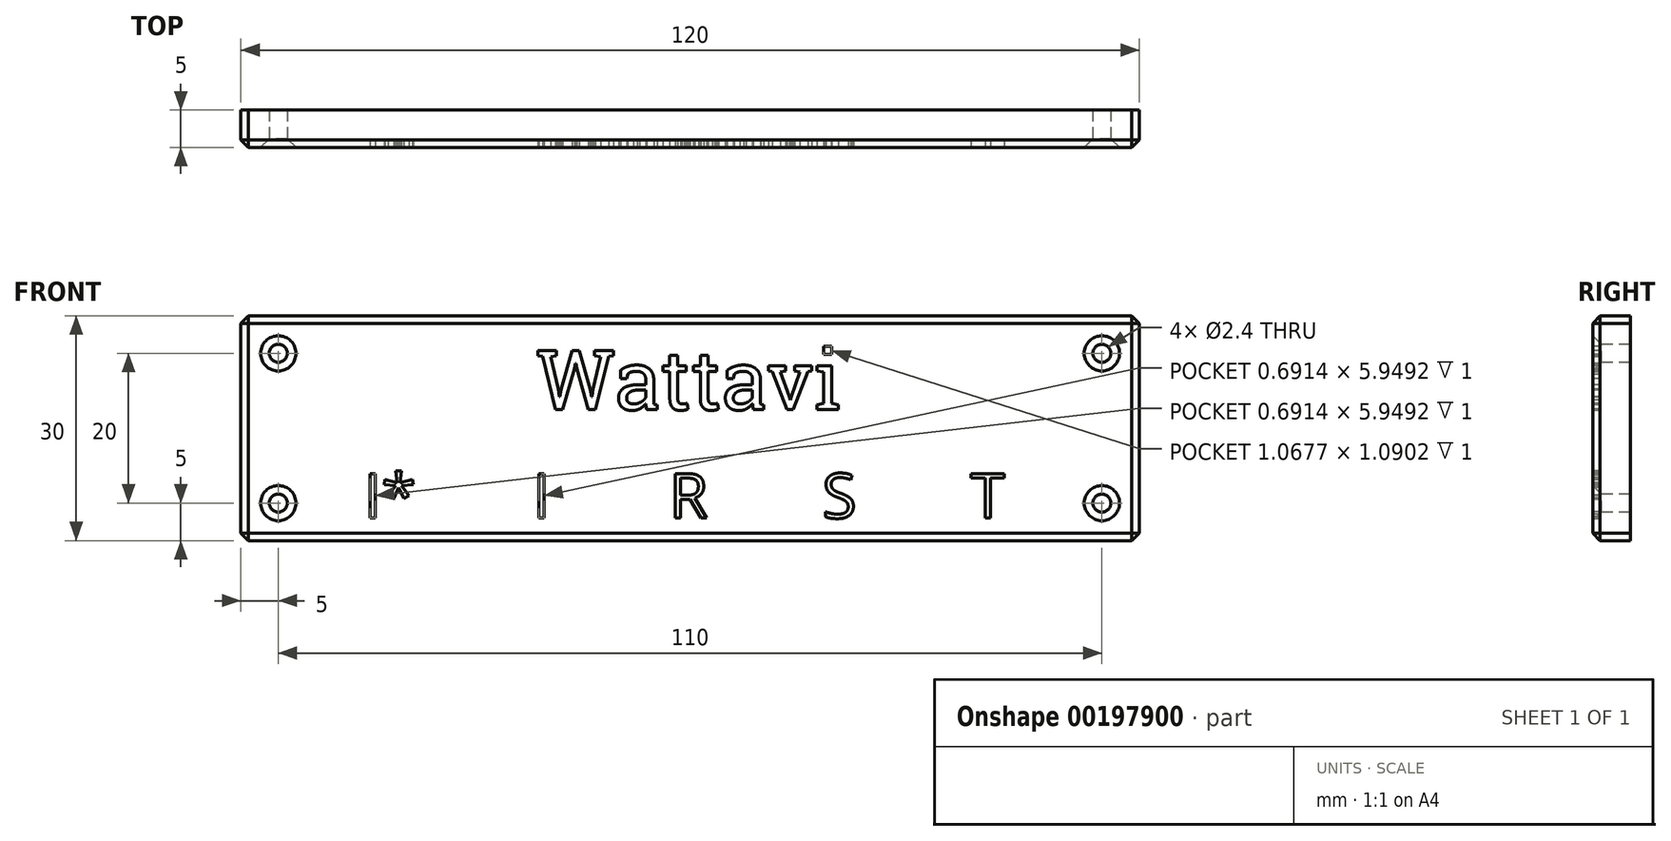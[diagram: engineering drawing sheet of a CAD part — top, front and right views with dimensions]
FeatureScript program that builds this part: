
annotation { "Feature Type Name" : "Feature", "Feature Type Description" : "" }
export const myFeature = defineFeature(function(context is Context, id is Id, definition is map)
    precondition{}
    {
        {
            var Q0;
            Q0=qCreatedBy(makeId("Front.planeOp"),FACE);
            var sketch = newSketch(context, id + "F0", { "sketchPlane" : qUnion([Q0])});
            skLineSegment(sketch, "E0.bottom", {"start": v(60, 15) * mm, "end": v(-60, 15) * mm});
            skLineSegment(sketch, "E0.top", {"start": v(60, -15) * mm, "end": v(-60, -15) * mm});
            skLineSegment(sketch, "E0.left", {"start": v(60, 15) * mm, "end": v(60, -15) * mm});
            skLineSegment(sketch, "E0.right", {"start": v(-60, 15) * mm, "end": v(-60, -15) * mm});
            skPoint(sketch, "E0.middle", {"position": v(0, 0) * mm});
            skSolve(sketch);
        }
        {
            var Q0;
            Q0=makeQuery(id+"F0.imprint","IMPRINT",FACE,{"disambiguationData":[TD([[makeQuery(id+"F0.imprint","IMPRINT",EDGE,{"derivedFrom":sQuery(id+"F0.wireOp",EDGE,"E0.bottom")}),1.0]])]});
            extrude(context, id + "F1", {"entities" : qUnion([Q0]), "depth" : 5 * mm, "symmetric" : true});
        }
        {
            var Q0;
            Q0=makeQuery(id+"F1.opExtrude","CAP_FACE",FACE,{"disambiguationData":[OSD([sQuery(id+"F0.wireOp",EDGE,"E0.bottom"),sQuery(id+"F0.wireOp",EDGE,"E0.top"),sQuery(id+"F0.wireOp",EDGE,"E0.left"),sQuery(id+"F0.wireOp",EDGE,"E0.right")])],"isStart":false});
            var Q1;
            Q1=makeQuery(id+"F1.opExtrude","SWEPT_EDGE",EDGE,{"disambiguationData":[OSD([sQuery(id+"F0.wireOp",EDGE,"E0.bottom"),sQuery(id+"F0.wireOp",EDGE,"E0.left")])]});
            var Q2;
            Q2=makeQuery(id+"F1.opExtrude","SWEPT_EDGE",EDGE,{"disambiguationData":[OSD([sQuery(id+"F0.wireOp",EDGE,"E0.bottom"),sQuery(id+"F0.wireOp",EDGE,"E0.right")])]});
            var Q3;
            Q3=makeQuery(id+"F1.opExtrude","SWEPT_EDGE",EDGE,{"disambiguationData":[OSD([sQuery(id+"F0.wireOp",EDGE,"E0.top"),sQuery(id+"F0.wireOp",EDGE,"E0.left")])]});
            var Q4;
            Q4=makeQuery(id+"F1.opExtrude","SWEPT_EDGE",EDGE,{"disambiguationData":[OSD([sQuery(id+"F0.wireOp",EDGE,"E0.top"),sQuery(id+"F0.wireOp",EDGE,"E0.right")])]});
            chamfer(context, id + "F2", {"entities" : qUnion([Q0, Q1, Q2, Q3, Q4]), "width" : 1 * mm, "tangentPropagation" : true});
        }
        {
            var Q0;
            Q0=makeQuery(id+"F1.opExtrude","CAP_FACE",FACE,{"disambiguationData":[OSD([sQuery(id+"F0.wireOp",EDGE,"E0.bottom"),sQuery(id+"F0.wireOp",EDGE,"E0.top"),sQuery(id+"F0.wireOp",EDGE,"E0.left"),sQuery(id+"F0.wireOp",EDGE,"E0.right")])],"isStart":false});
            var sketch = newSketch(context, id + "F3", { "sketchPlane" : qUnion([Q0])});
            skPoint(sketch, "E1", {"position": v(-55, 10) * mm});
            skPoint(sketch, "E2.MirrorP", {"position": v(55, 10) * mm});
            skPoint(sketch, "E3.MirrorP", {"position": v(-55, -10) * mm});
            skPoint(sketch, "E4.MirrorP", {"position": v(55, -10) * mm});
            skSolve(sketch);
        }
        {
            var Q0;
            Q0=sQuery(id+"F3.wireOp",VERTEX,"E2.MirrorP");
            var Q1;
            Q1=sQuery(id+"F3.wireOp",VERTEX,"E4.MirrorP");
            var Q2;
            Q2=sQuery(id+"F3.wireOp",VERTEX,"E3.MirrorP");
            var Q3;
            Q3=sQuery(id+"F3.wireOp",VERTEX,"E1");
            var Q4;
            Q4=makeQuery(id+"F1.opExtrude","SWEPT_BODY",BODY,{"disambiguationData":[OSD([sQuery(id+"F0.wireOp",EDGE,"E0.bottom"),sQuery(id+"F0.wireOp",EDGE,"E0.top"),sQuery(id+"F0.wireOp",EDGE,"E0.left"),sQuery(id+"F0.wireOp",EDGE,"E0.right")])]});
            hole(context, id + "F4", {"style" : HoleStyle.C_SINK, "endStyle" : HoleEndStyle.THROUGH, "standardTappedOrClearance" : lookupTablePath({ "fit" : "Normal", "standard" : "ISO", "size" : "M2", "type" : "Clearance" }), "standardBlindInLast" : lookupTablePath({ "fit" : "Normal", "standard" : "ISO", "engagement" : "75%", "pitch" : "0.4 mm", "size" : "M2", "type" : "Clearance & tapped" }), "holeDiameter" : 2.4 * mm, "cSinkDiameter" : 4.7 * mm, "cSinkAngle" : 90 * degree, "majorDiameter" : 5 * mm, "startFromSketch" : true, "locations" : qUnion([Q0, Q1, Q2, Q3]), "scope" : qUnion([Q4]), "isTappedThrough" : true, "tappedDepth" : 12 * mm, "tapClearance" : 3});
        }
        {
            var Q0;
            {var subQ0=sQuery(id+"F0.wireOp",EDGE,"E0.right");var subQ2=sQuery(id+"F0.wireOp",EDGE,"E0.left");var subQ6=sQuery(id+"F0.wireOp",EDGE,"E0.top");var subQ7=makeQuery(id+"F2.opChamfer","BLEND_FACE",FACE,{"disambiguationData":[OSD([subQ6])]});var subQ8=sQuery(id+"F0.wireOp",EDGE,"E0.bottom");var subQ9=makeQuery(id+"F2.opChamfer","BLEND_FACE",FACE,{"disambiguationData":[OSD([subQ8])]});Q0=makeQuery(id+"F4.hole-3.boolean.opBoolean","SPLIT",FACE,{"disambiguationData":[TD([subQ7])],"derivedFrom":makeQuery(id+"F4.hole-2.boolean.opBoolean","SPLIT",FACE,{"disambiguationData":[TD([subQ9])],"derivedFrom":makeQuery(id+"F4.hole-1.boolean.opBoolean","SPLIT",FACE,{"disambiguationData":[TD([subQ9])],"derivedFrom":makeQuery(id+"F4.hole-0.boolean.opBoolean","SPLIT",FACE,{"disambiguationData":[TD([subQ7])],"derivedFrom":makeQuery(id+"F1.opExtrude","CAP_FACE",FACE,{"disambiguationData":[OSD([subQ8,subQ6,subQ2,subQ0])],"isStart":false})})})})});}
            var sketch = newSketch(context, id + "F5", { "sketchPlane" : qUnion([Q0])});
            skText(sketch, "E5", { "text": "Wattavi", "fontName": "RobotoSlab-Regular.ttf"});
            skText(sketch, "E6", { "text": "I*", "fontName": "OpenSans-Regular.ttf"});
            skText(sketch, "E7", { "text": "I", "fontName": "OpenSans-Regular.ttf"});
            skText(sketch, "E8", { "text": "R", "fontName": "OpenSans-Regular.ttf"});
            skText(sketch, "E9", { "text": "S", "fontName": "OpenSans-Regular.ttf"});
            skText(sketch, "E10", { "text": "T", "fontName": "OpenSans-Regular.ttf"});
            const initialGuessF5  = {"E5": [-0.02048, 0.00247, 1, 0, 0.008], "E6": [-0.04354, -0.012, 1, 0, 0.006], "E7": [-0.02102, -0.012, 1, 0, 0.006], "E8": [-0.00277, -0.012, 1, 0, 0.006], "E9": [0.01764, -0.012, 1, 0, 0.006], "E10": [0.03746, -0.012, 1, 0, 0.006]};
            skSetInitialGuess(sketch, initialGuessF5);
            skSolve(sketch);
        }
        {
            var Q0;
            Q0 = qSketchRegion(id + "F5", true);
            extrude(context, id + "F6", {"entities" : qUnion([Q0]), "operationType" : NewBodyOperationType.REMOVE, "oppositeDirection" : true, "depth" : 1 * mm});
        }
    });
